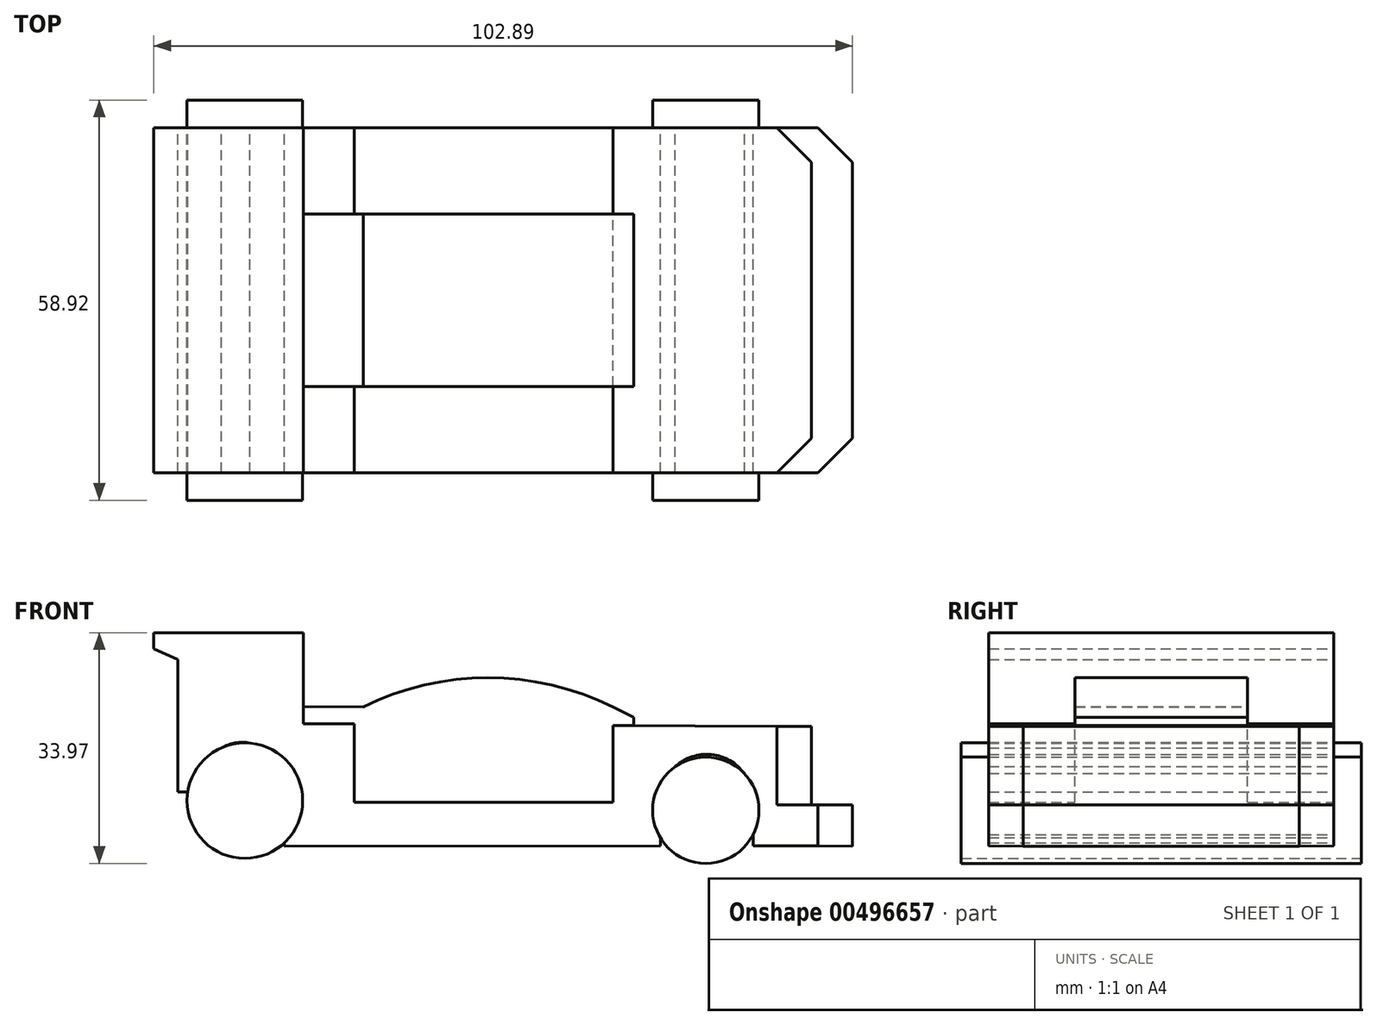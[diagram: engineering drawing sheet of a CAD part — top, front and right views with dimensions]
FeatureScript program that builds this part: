
annotation { "Feature Type Name" : "Feature", "Feature Type Description" : "" }
export const myFeature = defineFeature(function(context is Context, id is Id, definition is map)
    precondition{}
    {
        {
            var Q0;
            Q0=qCreatedBy(makeId("Front.planeOp"),FACE);
            var sketch = newSketch(context, id + "F0", { "sketchPlane" : qUnion([Q0])});
            skPoint(sketch, "E0.middle", {"position": v(0, 0) * mm});
            skLineSegment(sketch, "E1", {"start": v(-28.03, -14.08) * mm, "end": v(27.3, -14.02) * mm});
            skLineSegment(sketch, "E2", {"start": v(55.6, -14.06) * mm, "end": v(40.96, -14.02) * mm});
            skLineSegment(sketch, "E3", {"start": v(-47.29, 17.37) * mm, "end": v(-47.29, 14.99) * mm});
            skLineSegment(sketch, "E4", {"start": v(-17.79, -7.58) * mm, "end": v(20.31, -7.58) * mm});
            skLineSegment(sketch, "E5", {"start": v(55.6, -14.06) * mm, "end": v(55.6, -8) * mm});
            skLineSegment(sketch, "E6", {"start": v(55.6, -8) * mm, "end": v(49.56, -8) * mm});
            skLineSegment(sketch, "E7", {"start": v(49.56, -8) * mm, "end": v(49.56, 3.55) * mm});
            skLineSegment(sketch, "E8", {"start": v(49.56, 3.55) * mm, "end": v(-25.27, 3.98) * mm});
            skLineSegment(sketch, "E9", {"start": v(-25.27, 17.37) * mm, "end": v(-25.27, 3.98) * mm});
            skLineSegment(sketch, "E10", {"start": v(-17.79, -7.58) * mm, "end": v(-17.79, 3.93) * mm});
            skLineSegment(sketch, "E11", {"start": v(20.31, -7.58) * mm, "end": v(20.31, 3.71) * mm});
            skLineSegment(sketch, "E12", {"start": v(27.3, -14.02) * mm, "end": v(27.3, -7.38) * mm});
            skLineSegment(sketch, "E13", {"start": v(40.96, -14.02) * mm, "end": v(40.96, -7.38) * mm});
            skArc(sketch, "E14", {"start": v(40.96, -7.38) * mm, "mid": v(34.13, -0.55) * mm, "end": v(27.3, -7.38) * mm});
            skLineSegment(sketch, "E15", {"start": v(-28.03, -14.08) * mm, "end": v(-28.03, -4.31) * mm});
            skLineSegment(sketch, "E16", {"start": v(-40.49, -6.05) * mm, "end": v(-40.49, -4.31) * mm});
            skLineSegment(sketch, "E17", {"start": v(-47.29, 14.99) * mm, "end": v(-43.72, 13.4) * mm});
            skLineSegment(sketch, "E18", {"start": v(-43.72, 13.4) * mm, "end": v(-43.72, -6.05) * mm});
            skLineSegment(sketch, "E19", {"start": v(-43.72, -6.05) * mm, "end": v(-40.49, -6.05) * mm});
            skLineSegment(sketch, "E20", {"start": v(-25.27, 17.37) * mm, "end": v(-47.29, 17.37) * mm});
            skArc(sketch, "E21", {"start": v(-28.03, -4.31) * mm, "mid": v(-34.26, 1.22) * mm, "end": v(-40.49, -4.31) * mm});
            skLineSegment(sketch, "E22", {"start": v(-25.27, 3.98) * mm, "end": v(-16.47, 3.93) * mm});
            skLineSegment(sketch, "E23", {"start": v(-16.47, 3.93) * mm, "end": v(-16.47, 6.42) * mm});
            skLineSegment(sketch, "E24", {"start": v(-16.47, 6.42) * mm, "end": v(-25.27, 6.47) * mm});
            skLineSegment(sketch, "E25", {"start": v(20.31, 3.71) * mm, "end": v(20.31, 6.42) * mm});
            skArc(sketch, "E26", {"start": v(20.31, 6.42) * mm, "mid": v(1.92, 10.73) * mm, "end": v(-16.47, 6.42) * mm});
            skLineSegment(sketch, "E27", {"start": v(20.31, 6.42) * mm, "end": v(23.39, 4.9) * mm});
            skLineSegment(sketch, "E28", {"start": v(23.39, 4.9) * mm, "end": v(23.39, 3.71) * mm});
            skLineSegment(sketch, "E29", {"start": v(1.92, 10.73) * mm, "end": v(1.92, 3.82) * mm});
            skLineSegment(sketch, "E30", {"start": v(20.31, 6.42) * mm, "end": v(20.31, 3.71) * mm});
            skLineSegment(sketch, "E31", {"start": v(20.31, 3.71) * mm, "end": v(23.39, 3.71) * mm});
            skLineSegment(sketch, "E32", {"start": v(20.31, 3.71) * mm, "end": v(1.92, 3.82) * mm});
            skSolve(sketch);
        }
        {
            var Q0;
            {var subQ1=sQuery(id+"F0.wireOp",EDGE,"E1");Q0=makeQuery(id+"F0.imprint","IMPRINT",FACE,{"disambiguationData":[TD([[makeQuery(id+"F0.imprint","IMPRINT",EDGE,{"derivedFrom":subQ1}),1.0]])]});}
            extrude(context, id + "F1", {"entities" : qUnion([Q0]), "endBound" : BoundingType.SYMMETRIC, "depth" : 50.8 * mm});
        }
        {
            var Q0;
            Q0=makeQuery(id+"F0.imprint","IMPRINT",FACE,{"disambiguationData":[TD([[makeQuery(id+"F0.imprint","IMPRINT",EDGE,{"derivedFrom":sQuery(id+"F0.wireOp",EDGE,"E4")}),1.0]])]});
            var Q1;
            {var subQ0=sQuery(id+"F0.wireOp",EDGE,"E23");Q1=makeQuery(id+"F0.imprint","IMPRINT",FACE,{"disambiguationData":[TD([[makeQuery(id+"F0.imprint","IMPRINT",EDGE,{"derivedFrom":subQ0}),-1.0]])]});}
            var Q2;
            {var subQ0=sQuery(id+"F0.wireOp",EDGE,"E23");Q2=makeQuery(id+"F0.imprint","IMPRINT",FACE,{"disambiguationData":[TD([[makeQuery(id+"F0.imprint","IMPRINT",EDGE,{"derivedFrom":subQ0}),1.0]])]});}
            var Q3;
            {var subQ0=sQuery(id+"F0.wireOp",EDGE,"E25");Q3=makeQuery(id+"F0.imprint","IMPRINT",FACE,{"disambiguationData":[TD([[makeQuery(id+"F0.imprint","IMPRINT",EDGE,{"derivedFrom":subQ0}),1.0]])]});}
            var Q4;
            {var subQ2=sQuery(id+"F0.wireOp",EDGE,"E29");Q4=makeQuery(id+"F0.imprint","IMPRINT",FACE,{"disambiguationData":[TD([[makeQuery(id+"F0.imprint","IMPRINT",EDGE,{"derivedFrom":subQ2}),1.0]])]});}
            var Q5;
            Q5=makeQuery(id+"F0.imprint","IMPRINT",FACE,{"disambiguationData":[TD([[makeQuery(id+"F0.imprint","IMPRINT",EDGE,{"derivedFrom":sQuery(id+"F0.wireOp",EDGE,"E27")}),-1.0]])]});
            extrude(context, id + "F2", {"entities" : qUnion([Q0, Q1, Q2, Q3, Q4, Q5]), "operationType" : NewBodyOperationType.ADD, "endBound" : BoundingType.SYMMETRIC, "depth" : 25.4 * mm});
        }
        {
            var Q0;
            Q0=makeQuery(id+"F1.opExtrude","CAP_EDGE",EDGE,{"disambiguationData":[OSD([sQuery(id+"F0.wireOp",EDGE,"E7")])],"isStart":true});
            var Q1;
            Q1=makeQuery(id+"F1.opExtrude","CAP_EDGE",EDGE,{"disambiguationData":[OSD([sQuery(id+"F0.wireOp",EDGE,"E5")])],"isStart":true});
            var Q2;
            Q2=makeQuery(id+"F1.opExtrude","CAP_EDGE",EDGE,{"disambiguationData":[OSD([sQuery(id+"F0.wireOp",EDGE,"E7")])],"isStart":false});
            var Q3;
            Q3=makeQuery(id+"F1.opExtrude","CAP_EDGE",EDGE,{"disambiguationData":[OSD([sQuery(id+"F0.wireOp",EDGE,"E5")])],"isStart":false});
            chamfer(context, id + "F3", {"entities" : qUnion([Q0, Q1, Q2, Q3]), "width" : 5.08 * mm, "tangentPropagation" : true});
        }
        {
            var Q0;
            Q0=qCreatedBy(makeId("Front.planeOp"),FACE);
            var sketch = newSketch(context, id + "F4", { "sketchPlane" : qUnion([Q0])});
            skCircle(sketch, "E33", {"center": v(33.99, -8.77) * mm, "radius": 7.83 * mm});
            skPoint(sketch, "E33.first.point", {"position": v(34.56, -16.58) * mm});
            skPoint(sketch, "E33.second.point", {"position": v(39.44, -3.15) * mm});
            skPoint(sketch, "E33.third.point", {"position": v(30.8, -1.63) * mm});
            skCircle(sketch, "E34", {"center": v(-33.88, -7.36) * mm, "radius": 8.5 * mm});
            skPoint(sketch, "E34.first.point", {"position": v(-34.54, 1.12) * mm});
            skPoint(sketch, "E34.second.point", {"position": v(-33.82, -15.87) * mm});
            skPoint(sketch, "E34.third.point", {"position": v(-25.99, -4.17) * mm});
            skSolve(sketch);
        }
        {
            var Q0;
            Q0=makeQuery(id+"F4.imprint","IMPRINT",FACE,{"disambiguationData":[TD([[makeQuery(id+"F4.imprint","IMPRINT",EDGE,{"derivedFrom":sQuery(id+"F4.wireOp",EDGE,"E34")}),1.0]])]});
            var Q1;
            Q1=makeQuery(id+"F4.imprint","IMPRINT",FACE,{"disambiguationData":[TD([[makeQuery(id+"F4.imprint","IMPRINT",EDGE,{"derivedFrom":sQuery(id+"F4.wireOp",EDGE,"E33")}),1.0]])]});
            extrude(context, id + "F5", {"entities" : qUnion([Q0, Q1]), "operationType" : NewBodyOperationType.ADD, "endBound" : BoundingType.SYMMETRIC, "depth" : 58.93 * mm});
        }
    });
